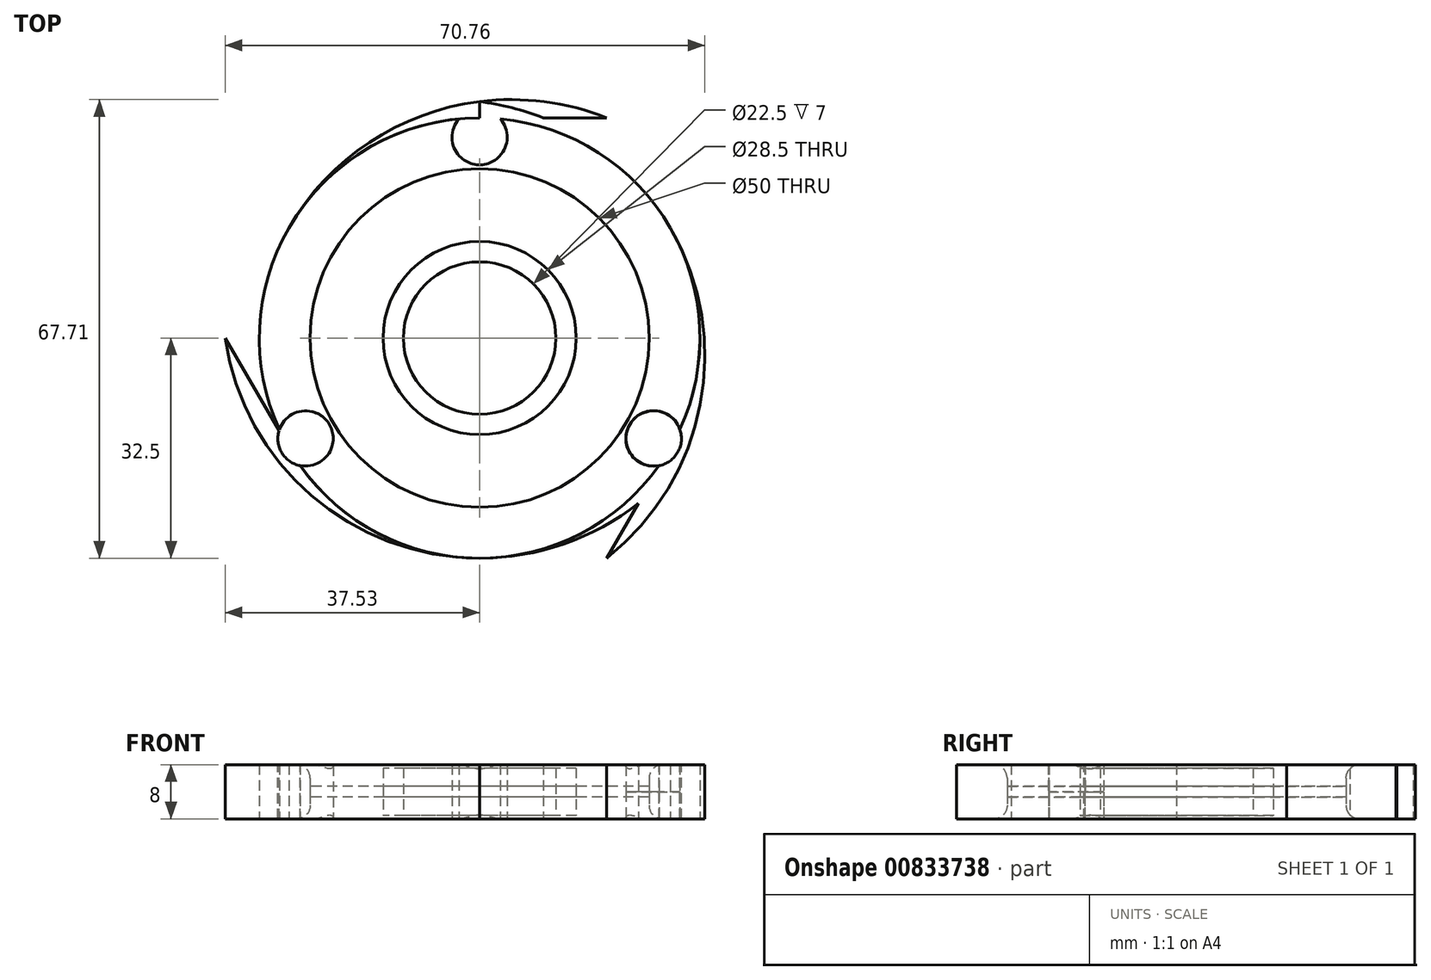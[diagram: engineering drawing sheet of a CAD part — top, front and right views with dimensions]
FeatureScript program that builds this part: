
annotation { "Feature Type Name" : "Feature", "Feature Type Description" : "" }
export const myFeature = defineFeature(function(context is Context, id is Id, definition is map)
    precondition{}
    {
        {
            var Q0;
            Q0=qCreatedBy(makeId("Top.planeOp"),FACE);
            var sketch = newSketch(context, id + "F0", { "sketchPlane" : qUnion([Q0])});
            skCircle(sketch, "E0", {"center": v(0, 0) * mm, "radius": 11.25 * mm});
            skCircle(sketch, "E1", {"center": v(0, 0) * mm, "radius": 14.25 * mm});
            skCircle(sketch, "E2", {"center": v(0, 0) * mm, "radius": 32.5 * mm});
            skCircle(sketch, "E3", {"center": v(0, 0) * mm, "radius": 25 * mm});
            skCircle(sketch, "E4.cCircle", {"center": v(0, 0) * mm, "radius": 32.5 * mm, "construction": true});
            skLineSegment(sketch, "E4.0", {"start": v(18.76, -32.5) * mm, "end": v(-18.76, -32.5) * mm});
            skLineSegment(sketch, "E4.1", {"start": v(-18.76, -32.5) * mm, "end": v(-37.53, 0) * mm});
            skLineSegment(sketch, "E4.2", {"start": v(-37.53, 0) * mm, "end": v(-18.76, 32.5) * mm});
            skLineSegment(sketch, "E4.3", {"start": v(-18.76, 32.5) * mm, "end": v(18.76, 32.5) * mm});
            skLineSegment(sketch, "E4.4", {"start": v(18.76, 32.5) * mm, "end": v(37.53, 0) * mm});
            skLineSegment(sketch, "E4.5", {"start": v(37.53, 0) * mm, "end": v(18.76, -32.5) * mm});
            skPoint(sketch, "E4.0.midPoint", {"position": v(0, -32.5) * mm});
            skArc(sketch, "E5", {"start": v(18.76, -32.5) * mm, "mid": v(28.15, 16.25) * mm, "end": v(-18.76, 32.5) * mm});
            skArc(sketch, "E6", {"start": v(-37.53, 0) * mm, "mid": v(0, -32.5) * mm, "end": v(37.53, 0) * mm});
            skArc(sketch, "E7", {"start": v(18.76, 32.5) * mm, "mid": v(-28.15, 16.25) * mm, "end": v(-18.76, -32.5) * mm});
            skLineSegment(sketch, "E8", {"start": v(0, 0) * mm, "end": v(0, 34.92) * mm});
            skPoint(sketch, "E8.endSnap0", {"position": v(0, 32.5) * mm});
            skCircle(sketch, "E9", {"center": v(0, 29.65) * mm, "radius": 4.08 * mm});
            skCircle(sketch, "E10.1.0", {"center": v(-25.68, -14.82) * mm, "radius": 4.08 * mm});
            skCircle(sketch, "E10.2.0", {"center": v(25.68, -14.82) * mm, "radius": 4.08 * mm});
            skSolve(sketch);
        }
        {
            var Q0;
            {var subQ2=sQuery(id+"F0.wireOp",EDGE,"ea3b9ac0-2b91-4825-b409-2e6de5cae28a.2.1");var subQ5=sQuery(id+"F0.wireOp",EDGE,"E3");var subQ6=makeQuery(id+"F0.imprint","INTERSECT",VERTEX,{"disambiguationData":[OD(0.0)],"derivedFrom":[subQ5,subQ2]});Q0=makeQuery(id+"F0.imprint","IMPRINT",FACE,{"disambiguationData":[TD([[makeQuery(id+"F0.imprint","IMPRINT",EDGE,{"disambiguationData":[TD([[subQ6,1.0]])],"derivedFrom":subQ5}),-1.0]])]});}
            var Q1;
            {var subQ1=sQuery(id+"F0.wireOp",EDGE,"ea3b9ac0-2b91-4825-b409-2e6de5cae28a.2.1");var subQ7=sQuery(id+"F0.wireOp",EDGE,"E3");var subQ9=makeQuery(id+"F0.imprint","INTERSECT",VERTEX,{"disambiguationData":[OD(0.0)],"derivedFrom":[subQ7,subQ1]});Q1=makeQuery(id+"F0.imprint","IMPRINT",FACE,{"disambiguationData":[TD([[makeQuery(id+"F0.imprint","IMPRINT",EDGE,{"disambiguationData":[TD([[subQ9,-1.0]])],"derivedFrom":subQ7}),-1.0]])]});}
            var Q2;
            {var subQ2=sQuery(id+"F0.wireOp",EDGE,"ea3b9ac0-2b91-4825-b409-2e6de5cae28a.2.2");var subQ5=sQuery(id+"F0.wireOp",EDGE,"E3");var subQ6=makeQuery(id+"F0.imprint","INTERSECT",VERTEX,{"disambiguationData":[OD(0.0)],"derivedFrom":[subQ5,subQ2]});Q2=makeQuery(id+"F0.imprint","IMPRINT",FACE,{"disambiguationData":[TD([[makeQuery(id+"F0.imprint","IMPRINT",EDGE,{"disambiguationData":[TD([[subQ6,-1.0]])],"derivedFrom":subQ5}),-1.0]])]});}
            var Q3;
            {var subQ3=sQuery(id+"F0.wireOp",EDGE,"E3");var subQ6=sQuery(id+"F0.wireOp",EDGE,"ea3b9ac0-2b91-4825-b409-2e6de5cae28a.2.2");var subQ9=makeQuery(id+"F0.imprint","INTERSECT",VERTEX,{"disambiguationData":[OD(1.0)],"derivedFrom":[subQ3,subQ6]});Q3=makeQuery(id+"F0.imprint","IMPRINT",FACE,{"disambiguationData":[TD([[makeQuery(id+"F0.imprint","IMPRINT",EDGE,{"disambiguationData":[TD([[subQ9,-1.0]])],"derivedFrom":subQ3}),-1.0]])]});}
            var Q4;
            {var subQ2=sQuery(id+"F0.wireOp",EDGE,"ea3b9ac0-2b91-4825-b409-2e6de5cae28a.2.0");var subQ4=sQuery(id+"F0.wireOp",EDGE,"E3");var subQ5=makeQuery(id+"F0.imprint","INTERSECT",VERTEX,{"disambiguationData":[OD(0.0)],"derivedFrom":[subQ4,subQ2]});Q4=makeQuery(id+"F0.imprint","IMPRINT",FACE,{"disambiguationData":[TD([[makeQuery(id+"F0.imprint","IMPRINT",EDGE,{"disambiguationData":[TD([[subQ5,-1.0]])],"derivedFrom":subQ4}),-1.0]])]});}
            var Q5;
            {var subQ1=sQuery(id+"F0.wireOp",EDGE,"ea3b9ac0-2b91-4825-b409-2e6de5cae28a.2.1");var subQ3=sQuery(id+"F0.wireOp",EDGE,"E3");var subQ4=makeQuery(id+"F0.imprint","INTERSECT",VERTEX,{"disambiguationData":[OD(1.0)],"derivedFrom":[subQ3,subQ1]});Q5=makeQuery(id+"F0.imprint","IMPRINT",FACE,{"disambiguationData":[TD([[makeQuery(id+"F0.imprint","IMPRINT",EDGE,{"disambiguationData":[TD([[subQ4,1.0]])],"derivedFrom":subQ3}),-1.0]])]});}
            extrude(context, id + "F1", {"entities" : qUnion([Q0, Q1, Q2, Q3, Q4, Q5]), "depth" : 4 * mm, "offsetDistance" : 25 * mm, "hasSecondDirection" : true, "secondDirectionOppositeDirection" : true, "secondDirectionDepth" : 4 * mm});
        }
        {
            var Q0;
            Q0=makeQuery(id+"F0.imprint","IMPRINT",FACE,{"disambiguationData":[TD([[makeQuery(id+"F0.imprint","IMPRINT",EDGE,{"derivedFrom":sQuery(id+"F0.wireOp",EDGE,"E0")}),-1.0]])]});
            extrude(context, id + "F2", {"entities" : qUnion([Q0]), "depth" : 3.5 * mm, "offsetDistance" : 25 * mm, "hasSecondDirection" : true, "secondDirectionOppositeDirection" : true, "secondDirectionDepth" : 3.5 * mm});
        }
        {
            var Q0;
            {var subQ0=sQuery(id+"F0.wireOp",EDGE,"ea3b9ac0-2b91-4825-b409-2e6de5cae28a.2.2");var subQ1=sQuery(id+"F0.wireOp",EDGE,"E3");var subQ2=makeQuery(id+"F0.imprint","INTERSECT",VERTEX,{"disambiguationData":[OD(0.0)],"derivedFrom":[subQ1,subQ0]});Q0=makeQuery(id+"F0.imprint","IMPRINT",FACE,{"disambiguationData":[TD([[makeQuery(id+"F0.imprint","IMPRINT",EDGE,{"disambiguationData":[TD([[subQ2,-1.0]])],"derivedFrom":subQ1}),1.0]])]});}
            var Q1;
            Q1=makeQuery(id+"F0.imprint","IMPRINT",FACE,{"disambiguationData":[TD([[makeQuery(id+"F0.imprint","IMPRINT",EDGE,{"derivedFrom":sQuery(id+"F0.wireOp",EDGE,"E1")}),-1.0]])]});
            var Q2;
            {var subQ0=sQuery(id+"F0.wireOp",EDGE,"ea3b9ac0-2b91-4825-b409-2e6de5cae28a.2.1");var subQ1=sQuery(id+"F0.wireOp",EDGE,"E3");var subQ2=makeQuery(id+"F0.imprint","INTERSECT",VERTEX,{"disambiguationData":[OD(0.0)],"derivedFrom":[subQ1,subQ0]});Q2=makeQuery(id+"F0.imprint","IMPRINT",FACE,{"disambiguationData":[TD([[makeQuery(id+"F0.imprint","IMPRINT",EDGE,{"disambiguationData":[TD([[subQ2,1.0]])],"derivedFrom":subQ1}),1.0]])]});}
            var Q3;
            {var subQ0=sQuery(id+"F0.wireOp",EDGE,"ea3b9ac0-2b91-4825-b409-2e6de5cae28a.2.0");var subQ1=sQuery(id+"F0.wireOp",EDGE,"E3");var subQ2=makeQuery(id+"F0.imprint","INTERSECT",VERTEX,{"disambiguationData":[OD(0.0)],"derivedFrom":[subQ1,subQ0]});Q3=makeQuery(id+"F0.imprint","IMPRINT",FACE,{"disambiguationData":[TD([[makeQuery(id+"F0.imprint","IMPRINT",EDGE,{"disambiguationData":[TD([[subQ2,-1.0]])],"derivedFrom":subQ1}),1.0]])]});}
            extrude(context, id + "F3", {"entities" : qUnion([Q0, Q1, Q2, Q3]), "depth" : .8 * mm, "offsetDistance" : 25 * mm, "hasSecondDirection" : true, "secondDirectionOppositeDirection" : true, "secondDirectionDepth" : .8 * mm});
        }
        {
            var Q0;
            {var subQ0=sQuery(id+"F0.wireOp",EDGE,"E4.1");var subQ1=sQuery(id+"F0.wireOp",EDGE,"E2");var subQ2=makeQuery(id+"F0.imprint","INTERSECT",VERTEX,{"derivedFrom":[subQ1,subQ0]});Q0=makeQuery(id+"F0.imprint","IMPRINT",FACE,{"disambiguationData":[TD([[makeQuery(id+"F0.imprint","IMPRINT",EDGE,{"disambiguationData":[TD([[subQ2,-1.0]])],"derivedFrom":subQ0}),-1.0]])]});}
            var Q1;
            {var subQ0=sQuery(id+"F0.wireOp",EDGE,"E4.1");var subQ1=makeQuery(id+"F0.imprint","INTERSECT",VERTEX,{"derivedFrom":[sQuery(id+"F0.wireOp",EDGE,"E2"),subQ0]});Q1=makeQuery(id+"F0.imprint","IMPRINT",FACE,{"disambiguationData":[TD([[makeQuery(id+"F0.imprint","IMPRINT",EDGE,{"disambiguationData":[TD([[subQ1,1.0]])],"derivedFrom":subQ0}),1.0]])]});}
            var Q2;
            {var subQ0=sQuery(id+"F0.wireOp",EDGE,"E4.5");var subQ1=sQuery(id+"F0.wireOp",EDGE,"E2");var subQ2=makeQuery(id+"F0.imprint","INTERSECT",VERTEX,{"derivedFrom":[subQ1,subQ0]});Q2=makeQuery(id+"F0.imprint","IMPRINT",FACE,{"disambiguationData":[TD([[makeQuery(id+"F0.imprint","IMPRINT",EDGE,{"disambiguationData":[TD([[subQ2,-1.0]])],"derivedFrom":subQ0}),-1.0]])]});}
            var Q3;
            {var subQ0=sQuery(id+"F0.wireOp",EDGE,"E4.5");var subQ1=makeQuery(id+"F0.imprint","INTERSECT",VERTEX,{"derivedFrom":[sQuery(id+"F0.wireOp",EDGE,"E2"),subQ0]});Q3=makeQuery(id+"F0.imprint","IMPRINT",FACE,{"disambiguationData":[TD([[makeQuery(id+"F0.imprint","IMPRINT",EDGE,{"disambiguationData":[TD([[subQ1,1.0]])],"derivedFrom":subQ0}),1.0]])]});}
            var Q4;
            {var subQ0=sQuery(id+"F0.wireOp",EDGE,"E4.3");var subQ1=sQuery(id+"F0.wireOp",EDGE,"E2");var subQ2=makeQuery(id+"F0.imprint","INTERSECT",VERTEX,{"derivedFrom":[subQ1,subQ0]});Q4=makeQuery(id+"F0.imprint","IMPRINT",FACE,{"disambiguationData":[TD([[makeQuery(id+"F0.imprint","IMPRINT",EDGE,{"disambiguationData":[TD([[subQ2,-1.0]])],"derivedFrom":subQ0}),-1.0]])]});}
            var Q5;
            {var subQ1=sQuery(id+"F0.wireOp",EDGE,"E5");var subQ3=sQuery(id+"F0.wireOp",EDGE,"E4.5");var subQ4=makeQuery(id+"F0.imprint","INTERSECT",VERTEX,{"derivedFrom":[subQ3,subQ1]});Q5=makeQuery(id+"F0.imprint","IMPRINT",FACE,{"disambiguationData":[TD([[makeQuery(id+"F0.imprint","IMPRINT",EDGE,{"disambiguationData":[TD([[subQ4,-1.0]])],"derivedFrom":subQ3}),1.0]])]});}
            var Q6;
            {var subQ3=sQuery(id+"F0.wireOp",EDGE,"E5");var subQ5=sQuery(id+"F0.wireOp",EDGE,"E4.5");var subQ6=makeQuery(id+"F0.imprint","INTERSECT",VERTEX,{"derivedFrom":[subQ5,subQ3]});Q6=makeQuery(id+"F0.imprint","IMPRINT",FACE,{"disambiguationData":[TD([[makeQuery(id+"F0.imprint","IMPRINT",EDGE,{"disambiguationData":[TD([[subQ6,-1.0]])],"derivedFrom":subQ5}),-1.0]])]});}
            var Q7;
            {var subQ3=sQuery(id+"F0.wireOp",EDGE,"E7");var subQ5=sQuery(id+"F0.wireOp",EDGE,"E4.3");var subQ6=makeQuery(id+"F0.imprint","INTERSECT",VERTEX,{"derivedFrom":[subQ5,subQ3]});Q7=makeQuery(id+"F0.imprint","IMPRINT",FACE,{"disambiguationData":[TD([[makeQuery(id+"F0.imprint","IMPRINT",EDGE,{"disambiguationData":[TD([[subQ6,-1.0]])],"derivedFrom":subQ5}),-1.0]])]});}
            var Q8;
            {var subQ0=sQuery(id+"F0.wireOp",EDGE,"E9");var subQ1=sQuery(id+"F0.wireOp",EDGE,"E4.3");var subQ2=makeQuery(id+"F0.imprint","INTERSECT",VERTEX,{"disambiguationData":[OD(1.0)],"derivedFrom":[subQ1,subQ0]});Q8=makeQuery(id+"F0.imprint","IMPRINT",FACE,{"disambiguationData":[TD([[makeQuery(id+"F0.imprint","IMPRINT",EDGE,{"disambiguationData":[TD([[subQ2,-1.0]])],"derivedFrom":subQ0}),1.0]])]});}
            var Q9;
            {var subQ3=sQuery(id+"F0.wireOp",EDGE,"E6");var subQ5=sQuery(id+"F0.wireOp",EDGE,"E4.1");var subQ6=makeQuery(id+"F0.imprint","INTERSECT",VERTEX,{"derivedFrom":[subQ5,subQ3]});Q9=makeQuery(id+"F0.imprint","IMPRINT",FACE,{"disambiguationData":[TD([[makeQuery(id+"F0.imprint","IMPRINT",EDGE,{"disambiguationData":[TD([[subQ6,-1.0]])],"derivedFrom":subQ5}),-1.0]])]});}
            var Q10;
            {var subQ1=sQuery(id+"F0.wireOp",EDGE,"E6");var subQ3=sQuery(id+"F0.wireOp",EDGE,"E4.1");var subQ5=makeQuery(id+"F0.imprint","INTERSECT",VERTEX,{"derivedFrom":[subQ3,subQ1]});Q10=makeQuery(id+"F0.imprint","IMPRINT",FACE,{"disambiguationData":[TD([[makeQuery(id+"F0.imprint","IMPRINT",EDGE,{"disambiguationData":[TD([[subQ5,-1.0]])],"derivedFrom":subQ3}),1.0]])]});}
            var Q11;
            {var subQ0=sQuery(id+"F0.wireOp",EDGE,"E9");var subQ1=sQuery(id+"F0.wireOp",EDGE,"E4.3");var subQ2=makeQuery(id+"F0.imprint","INTERSECT",VERTEX,{"disambiguationData":[OD(0.0)],"derivedFrom":[subQ1,subQ0]});Q11=makeQuery(id+"F0.imprint","IMPRINT",FACE,{"disambiguationData":[TD([[makeQuery(id+"F0.imprint","IMPRINT",EDGE,{"disambiguationData":[TD([[subQ2,1.0]])],"derivedFrom":subQ0}),1.0]])]});}
            var Q12;
            {var subQ0=sQuery(id+"F0.wireOp",EDGE,"E7");var subQ1=sQuery(id+"F0.wireOp",EDGE,"E4.3");var subQ2=makeQuery(id+"F0.imprint","INTERSECT",VERTEX,{"derivedFrom":[subQ1,subQ0]});Q12=makeQuery(id+"F0.imprint","IMPRINT",FACE,{"disambiguationData":[TD([[makeQuery(id+"F0.imprint","IMPRINT",EDGE,{"disambiguationData":[TD([[subQ2,-1.0]])],"derivedFrom":subQ1}),1.0]])]});}
            var Q13;
            {var subQ0=sQuery(id+"F0.wireOp",EDGE,"E9");var subQ1=sQuery(id+"F0.wireOp",EDGE,"E4.3");var subQ2=makeQuery(id+"F0.imprint","INTERSECT",VERTEX,{"disambiguationData":[OD(1.0)],"derivedFrom":[subQ1,subQ0]});Q13=makeQuery(id+"F0.imprint","IMPRINT",FACE,{"disambiguationData":[TD([[makeQuery(id+"F0.imprint","IMPRINT",EDGE,{"disambiguationData":[TD([[subQ2,-1.0]])],"derivedFrom":subQ1}),1.0]])]});}
            var Q14;
            {var subQ0=sQuery(id+"F0.wireOp",EDGE,"E10.2.0");var subQ5=sQuery(id+"F0.wireOp",EDGE,"E4.5");var subQ6=makeQuery(id+"F0.imprint","INTERSECT",VERTEX,{"disambiguationData":[OD(1.0)],"derivedFrom":[subQ5,subQ0]});Q14=makeQuery(id+"F0.imprint","IMPRINT",FACE,{"disambiguationData":[TD([[makeQuery(id+"F0.imprint","IMPRINT",EDGE,{"disambiguationData":[TD([[subQ6,-1.0]])],"derivedFrom":subQ5}),-1.0]])]});}
            var Q15;
            {var subQ0=sQuery(id+"F0.wireOp",EDGE,"E5");var subQ3=sQuery(id+"F0.wireOp",EDGE,"E6");var subQ5=makeQuery(id+"F0.imprint","INTERSECT",VERTEX,{"derivedFrom":[subQ0,subQ3]});Q15=makeQuery(id+"F0.imprint","IMPRINT",FACE,{"disambiguationData":[TD([[makeQuery(id+"F0.imprint","IMPRINT",EDGE,{"disambiguationData":[TD([[subQ5,1.0]])],"derivedFrom":subQ3}),-1.0]])]});}
            var Q16;
            {var subQ0=sQuery(id+"F0.wireOp",EDGE,"E10.1.0");var subQ5=sQuery(id+"F0.wireOp",EDGE,"E4.1");var subQ6=makeQuery(id+"F0.imprint","INTERSECT",VERTEX,{"disambiguationData":[OD(1.0)],"derivedFrom":[subQ5,subQ0]});Q16=makeQuery(id+"F0.imprint","IMPRINT",FACE,{"disambiguationData":[TD([[makeQuery(id+"F0.imprint","IMPRINT",EDGE,{"disambiguationData":[TD([[subQ6,-1.0]])],"derivedFrom":subQ5}),-1.0]])]});}
            var Q17;
            {var subQ0=sQuery(id+"F0.wireOp",EDGE,"E6");var subQ3=sQuery(id+"F0.wireOp",EDGE,"E7");var subQ5=makeQuery(id+"F0.imprint","INTERSECT",VERTEX,{"derivedFrom":[subQ0,subQ3]});Q17=makeQuery(id+"F0.imprint","IMPRINT",FACE,{"disambiguationData":[TD([[makeQuery(id+"F0.imprint","IMPRINT",EDGE,{"disambiguationData":[TD([[subQ5,1.0]])],"derivedFrom":subQ3}),-1.0]])]});}
            var Q18;
            {var subQ0=sQuery(id+"F0.wireOp",EDGE,"E9");var subQ5=sQuery(id+"F0.wireOp",EDGE,"E4.3");var subQ6=makeQuery(id+"F0.imprint","INTERSECT",VERTEX,{"disambiguationData":[OD(1.0)],"derivedFrom":[subQ5,subQ0]});Q18=makeQuery(id+"F0.imprint","IMPRINT",FACE,{"disambiguationData":[TD([[makeQuery(id+"F0.imprint","IMPRINT",EDGE,{"disambiguationData":[TD([[subQ6,-1.0]])],"derivedFrom":subQ5}),-1.0]])]});}
            var Q19;
            {var subQ1=sQuery(id+"F0.wireOp",EDGE,"E4.3");var subQ3=sQuery(id+"F0.wireOp",EDGE,"E5");var subQ4=makeQuery(id+"F0.imprint","INTERSECT",VERTEX,{"derivedFrom":[subQ1,subQ3]});Q19=makeQuery(id+"F0.imprint","IMPRINT",FACE,{"disambiguationData":[TD([[makeQuery(id+"F0.imprint","IMPRINT",EDGE,{"disambiguationData":[TD([[subQ4,-1.0]])],"derivedFrom":subQ1}),1.0]])]});}
            extrude(context, id + "F4", {"entities" : qUnion([Q0, Q1, Q2, Q3, Q4, Q5, Q6, Q7, Q8, Q9, Q10, Q11, Q12, Q13, Q14, Q15, Q16, Q17, Q18, Q19]), "depth" : 4 * mm, "offsetDistance" : 25 * mm, "hasSecondDirection" : true, "secondDirectionOppositeDirection" : true, "secondDirectionDepth" : 4 * mm});
        }
        {
            var Q0;
            Q0=sQuery(id+"F0.wireOp",VERTEX,"E10.2.0.center");
            var Q1;
            Q1=makeQuery(id+"F4.opExtrude","SWEPT_BODY",BODY,{"disambiguationData":[OSD([sQuery(id+"F0.wireOp",EDGE,"E2"),sQuery(id+"F0.wireOp",EDGE,"E4.5"),sQuery(id+"F0.wireOp",EDGE,"E5"),sQuery(id+"F0.wireOp",EDGE,"E6"),sQuery(id+"F0.wireOp",EDGE,"E10.2.0")])]});
            hole(context, id + "F5", {"style" : HoleStyle.SIMPLE, "endStyle" : HoleEndStyle.THROUGH, "holeDiameter" : 8.2 * mm, "majorDiameter" : 5 * mm, "isTappedThrough" : true, "tappedDepth" : 12 * mm, "tapClearance" : 3, "startFromSketch" : true, "locations" : qUnion([Q0]), "scope" : qUnion([Q1])});
        }
        {
            var Q0;
            Q0=sQuery(id+"F0.wireOp",VERTEX,"E10.2.0.center");
            var Q1;
            Q1=makeQuery(id+"F4.opExtrude","SWEPT_BODY",BODY,{"disambiguationData":[OSD([sQuery(id+"F0.wireOp",EDGE,"E2"),sQuery(id+"F0.wireOp",EDGE,"E4.5"),sQuery(id+"F0.wireOp",EDGE,"E5"),sQuery(id+"F0.wireOp",EDGE,"E6"),sQuery(id+"F0.wireOp",EDGE,"E10.2.0")])]});
            var Q2;
            Q2=makeQuery(id+"F1.opExtrude","SWEPT_BODY",BODY,{"disambiguationData":[OSD([sQuery(id+"F0.wireOp",EDGE,"E3"),sQuery(id+"F0.wireOp",EDGE,"E2"),sQuery(id+"F0.wireOp",EDGE,"E9"),sQuery(id+"F0.wireOp",EDGE,"E10.1.0"),sQuery(id+"F0.wireOp",EDGE,"E10.2.0")])]});
            hole(context, id + "F6", {"style" : HoleStyle.SIMPLE, "endStyle" : HoleEndStyle.THROUGH, "oppositeDirection" : true, "holeDiameter" : 8.2 * mm, "majorDiameter" : 5 * mm, "isTappedThrough" : true, "tappedDepth" : 12 * mm, "tapClearance" : 3, "startFromSketch" : true, "locations" : qUnion([Q0]), "scope" : qUnion([Q1, Q2])});
        }
        {
            var Q0;
            Q0=sQuery(id+"F0.wireOp",VERTEX,"E9.center");
            var Q1;
            Q1=makeQuery(id+"F4.opExtrude","SWEPT_BODY",BODY,{"disambiguationData":[OSD([sQuery(id+"F0.wireOp",EDGE,"E2"),sQuery(id+"F0.wireOp",EDGE,"E4.3"),sQuery(id+"F0.wireOp",EDGE,"E5"),sQuery(id+"F0.wireOp",EDGE,"E7"),sQuery(id+"F0.wireOp",EDGE,"E9")])]});
            hole(context, id + "F7", {"style" : HoleStyle.SIMPLE, "endStyle" : HoleEndStyle.THROUGH, "holeDiameter" : 8.2 * mm, "majorDiameter" : 5 * mm, "isTappedThrough" : true, "tappedDepth" : 12 * mm, "tapClearance" : 3, "startFromSketch" : true, "locations" : qUnion([Q0]), "scope" : qUnion([Q1])});
        }
        {
            var Q0;
            Q0=sQuery(id+"F0.wireOp",VERTEX,"E9.center");
            var Q1;
            Q1=makeQuery(id+"F4.opExtrude","SWEPT_BODY",BODY,{"disambiguationData":[OSD([sQuery(id+"F0.wireOp",EDGE,"E2"),sQuery(id+"F0.wireOp",EDGE,"E4.3"),sQuery(id+"F0.wireOp",EDGE,"E5"),sQuery(id+"F0.wireOp",EDGE,"E7"),sQuery(id+"F0.wireOp",EDGE,"E9")])]});
            hole(context, id + "F8", {"style" : HoleStyle.SIMPLE, "endStyle" : HoleEndStyle.THROUGH, "oppositeDirection" : true, "holeDiameter" : 8.2 * mm, "majorDiameter" : 5 * mm, "isTappedThrough" : true, "tappedDepth" : 12 * mm, "tapClearance" : 3, "startFromSketch" : true, "locations" : qUnion([Q0]), "scope" : qUnion([Q1])});
        }
        {
            var Q0;
            Q0=sQuery(id+"F0.wireOp",VERTEX,"E10.1.0.center");
            var Q1;
            Q1=makeQuery(id+"F4.opExtrude","SWEPT_BODY",BODY,{"disambiguationData":[OSD([sQuery(id+"F0.wireOp",EDGE,"E2"),sQuery(id+"F0.wireOp",EDGE,"E4.1"),sQuery(id+"F0.wireOp",EDGE,"E6"),sQuery(id+"F0.wireOp",EDGE,"E7"),sQuery(id+"F0.wireOp",EDGE,"E10.1.0")])]});
            hole(context, id + "F9", {"style" : HoleStyle.SIMPLE, "endStyle" : HoleEndStyle.THROUGH, "holeDiameter" : 8.2 * mm, "majorDiameter" : 5 * mm, "isTappedThrough" : true, "tappedDepth" : 12 * mm, "tapClearance" : 3, "startFromSketch" : true, "locations" : qUnion([Q0]), "scope" : qUnion([Q1])});
        }
        {
            var Q0;
            Q0=sQuery(id+"F0.wireOp",VERTEX,"E10.1.0.center");
            var Q1;
            Q1=makeQuery(id+"F4.opExtrude","SWEPT_BODY",BODY,{"disambiguationData":[OSD([sQuery(id+"F0.wireOp",EDGE,"E2"),sQuery(id+"F0.wireOp",EDGE,"E4.1"),sQuery(id+"F0.wireOp",EDGE,"E6"),sQuery(id+"F0.wireOp",EDGE,"E7"),sQuery(id+"F0.wireOp",EDGE,"E10.1.0")])]});
            hole(context, id + "F10", {"style" : HoleStyle.SIMPLE, "endStyle" : HoleEndStyle.THROUGH, "oppositeDirection" : true, "holeDiameter" : 8.2 * mm, "majorDiameter" : 5 * mm, "isTappedThrough" : true, "tappedDepth" : 12 * mm, "tapClearance" : 3, "startFromSketch" : true, "locations" : qUnion([Q0]), "scope" : qUnion([Q1])});
        }
        {
            var Q0;
            Q0=makeQuery(id+"F1.opExtrude","SWEPT_FACE",FACE,{"disambiguationData":[OSD([sQuery(id+"F0.wireOp",EDGE,"E3")])]});
            fillet(context, id + "F11", {"entities" : qUnion([Q0]), "radius" : 2 * mm, "tangentPropagation" : true, "allowEdgeOverflow" : false});
        }
    });
